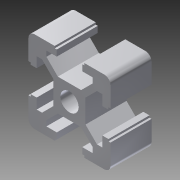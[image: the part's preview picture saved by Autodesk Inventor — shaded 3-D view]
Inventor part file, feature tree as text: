
AUTODESK INVENTOR PART (.ipt)
format: ipt  version: 2015 SP1 (Build 190203100, 203)  size: 156,672 bytes
history: native  units: mm
features: extrude x2, mirror x2, sketch x2, fillet x1
ambient origin geometry x8: Origin, YZ Plane, XZ Plane, XY Plane, X Axis, Y Axis, Z Axis, Center Point
bodies: Solid1 (feature_tree)
feature tree (7):
  extrude  "Extrusion1"  Depth=10.0mm
  fillet  "Fillet1"  Radius=10.0mm
  mirror  "Mirror1"
  mirror  "Mirror2"
  extrude  "Extrusion2"  Depth=6.1mm
  sketch  "Sketch1"  dims[d0=45.0deg d1=5.63mm d2=10.0mm]
  sketch  "Sketch2"  dims[d3=3.1mm d5=6.1mm d6=1.5mm d7=2.0mm d8=10.0mm d9=0.0mm d10=1.5mm d11=3.6mm d12=4.45mm d13=10.0mm d14=0.0mm]
